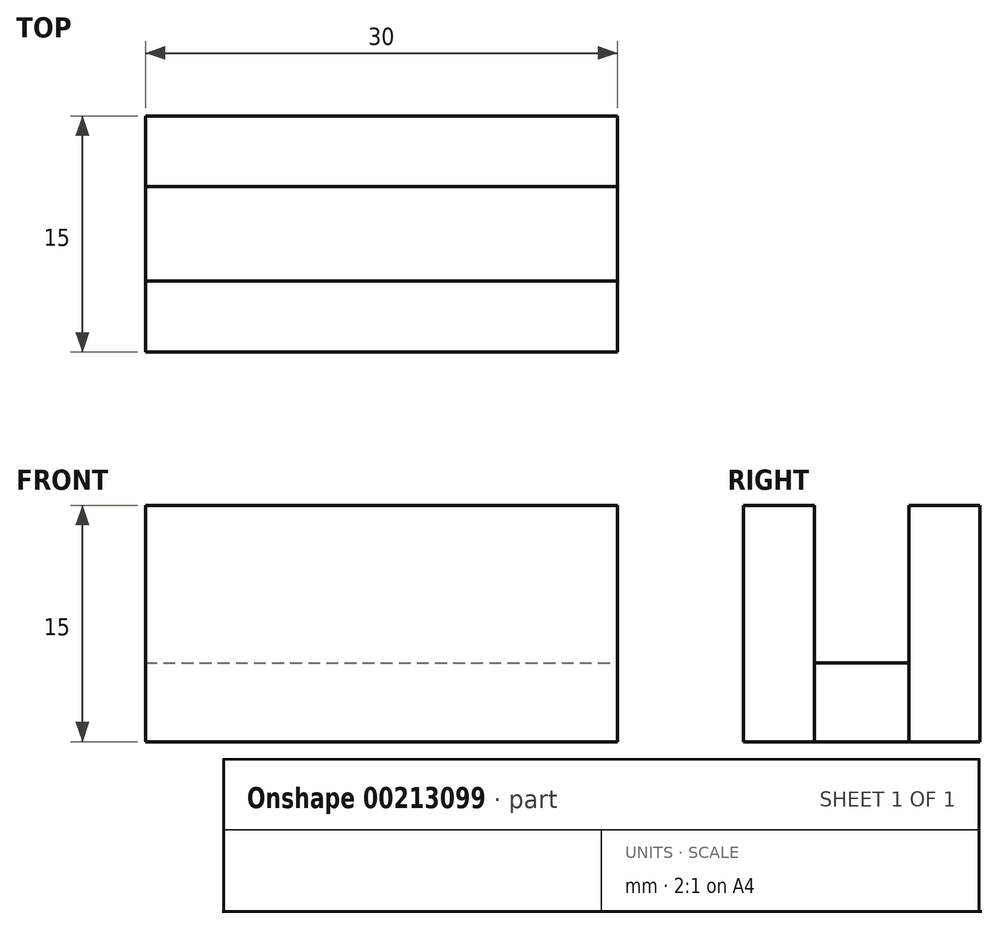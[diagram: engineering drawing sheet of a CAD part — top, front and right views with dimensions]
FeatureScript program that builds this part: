
annotation { "Feature Type Name" : "Feature", "Feature Type Description" : "" }
export const myFeature = defineFeature(function(context is Context, id is Id, definition is map)
    precondition{}
    {
        {
            var Q0;
            Q0=qCreatedBy(makeId("Top.planeOp"),FACE);
            var sketch = newSketch(context, id + "F0", { "sketchPlane" : qUnion([Q0])});
            skLineSegment(sketch, "E0.bottom", {"start": v(-15, 7.5) * mm, "end": v(15, 7.5) * mm});
            skLineSegment(sketch, "E0.top", {"start": v(-15, -7.5) * mm, "end": v(15, -7.5) * mm});
            skLineSegment(sketch, "E0.left", {"start": v(-15, 7.5) * mm, "end": v(-15, -7.5) * mm});
            skLineSegment(sketch, "E0.right", {"start": v(15, 7.5) * mm, "end": v(15, -7.5) * mm});
            skPoint(sketch, "E0.middle", {"position": v(0, 0) * mm});
            skLineSegment(sketch, "E1", {"start": v(-15, -3) * mm, "end": v(15, -3) * mm});
            skLineSegment(sketch, "E2", {"start": v(-15, 3) * mm, "end": v(15, 3) * mm});
            skSolve(sketch);
        }
        {
            var Q0;
            {var subQ0=sQuery(id+"F0.wireOp",EDGE,"E0.bottom");Q0=makeQuery(id+"F0.imprint","IMPRINT",FACE,{"disambiguationData":[TD([[makeQuery(id+"F0.imprint","IMPRINT",EDGE,{"derivedFrom":subQ0}),-1.0]])]});}
            var Q1;
            {var subQ0=sQuery(id+"F0.wireOp",EDGE,"E0.top");Q1=makeQuery(id+"F0.imprint","IMPRINT",FACE,{"disambiguationData":[TD([[makeQuery(id+"F0.imprint","IMPRINT",EDGE,{"derivedFrom":subQ0}),1.0]])]});}
            extrude(context, id + "F1", {"entities" : qUnion([Q0, Q1]), "depth" : 15 * mm});
        }
        {
            var Q0;
            {var subQ0=sQuery(id+"F0.wireOp",EDGE,"E1");Q0=makeQuery(id+"F0.imprint","IMPRINT",FACE,{"disambiguationData":[TD([[makeQuery(id+"F0.imprint","IMPRINT",EDGE,{"derivedFrom":subQ0}),1.0]])]});}
            extrude(context, id + "F2", {"entities" : qUnion([Q0]), "depth" : 5 * mm});
        }
    });
